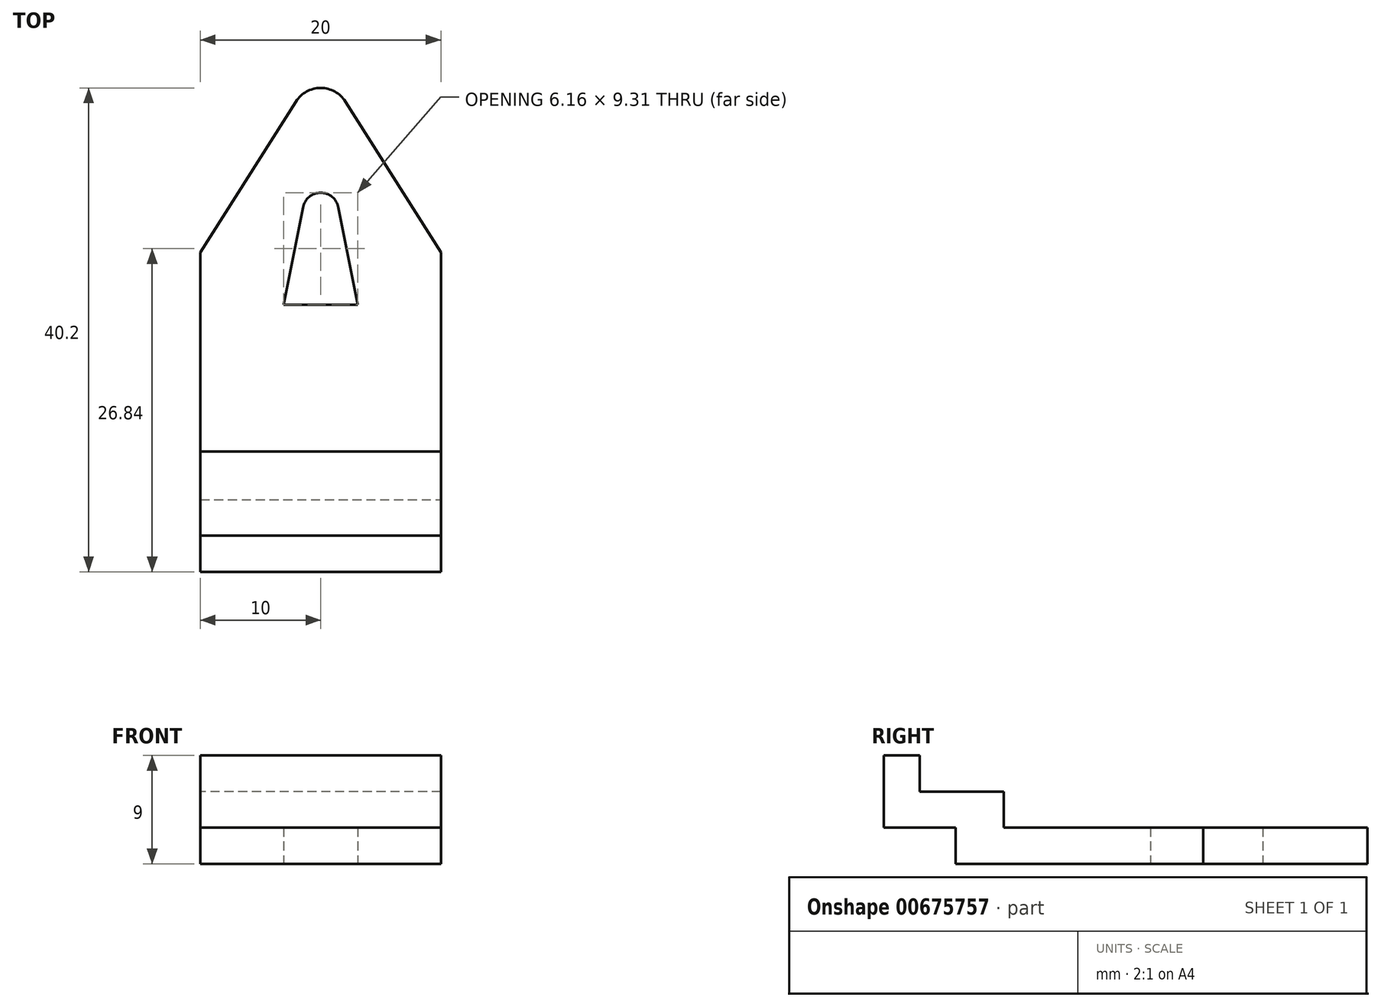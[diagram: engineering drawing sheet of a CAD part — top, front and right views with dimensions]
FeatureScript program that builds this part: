
annotation { "Feature Type Name" : "Feature", "Feature Type Description" : "" }
export const myFeature = defineFeature(function(context is Context, id is Id, definition is map)
    precondition{}
    {
        {
            var Q0;
            Q0=qCreatedBy(makeId("Top.planeOp"),FACE);
            var sketch = newSketch(context, id + "F0", { "sketchPlane" : qUnion([Q0])});
            skLineSegment(sketch, "E0", {"start": v(-2.06, -3.26) * mm, "end": v(-10, -15.78) * mm});
            skLineSegment(sketch, "E1", {"start": v(-10, -15.78) * mm, "end": v(-10, -42.32) * mm});
            skLineSegment(sketch, "E2", {"start": v(-10, -42.32) * mm, "end": v(0, -42.32) * mm});
            skArc(sketch, "E3", {"start": v(1.47, -12.03) * mm, "mid": v(0, -10.82) * mm, "end": v(-1.47, -12.03) * mm});
            skLineSegment(sketch, "E4.MirrorCS", {"start": v(10, -42.32) * mm, "end": v(0, -42.32) * mm});
            skLineSegment(sketch, "E5.MirrorCS", {"start": v(2.06, -3.26) * mm, "end": v(10, -15.78) * mm});
            skLineSegment(sketch, "E6.MirrorCS", {"start": v(10, -15.78) * mm, "end": v(10, -42.32) * mm});
            skArc(sketch, "E7", {"start": v(2.06, -3.26) * mm, "mid": v(0, -2.12) * mm, "end": v(-2.06, -3.26) * mm});
            skPoint(sketch, "E8.orphan", {"position": v(0, 0) * mm});
            skLineSegment(sketch, "E9", {"start": v(-1.47, -12.03) * mm, "end": v(-3.08, -20.14) * mm});
            skLineSegment(sketch, "E10", {"start": v(1.47, -12.03) * mm, "end": v(3.08, -20.14) * mm});
            skLineSegment(sketch, "E11", {"start": v(3.08, -20.14) * mm, "end": v(-3.08, -20.14) * mm});
            skSolve(sketch);
        }
        {
            var Q0;
            Q0=makeQuery(id+"F0.imprint","IMPRINT",FACE,{"disambiguationData":[TD([[makeQuery(id+"F0.imprint","IMPRINT",EDGE,{"derivedFrom":sQuery(id+"F0.wireOp",EDGE,"E0")}),1.0]])]});
            extrude(context, id + "F1", {"entities" : qUnion([Q0]), "depth" : 3 * mm, "offsetDistance" : 25 * mm});
        }
        {
            var Q0;
            Q0=makeQuery(id+"F1.opExtrude","CAP_FACE",FACE,{"disambiguationData":[OSD([sQuery(id+"F0.wireOp",EDGE,"E0"),sQuery(id+"F0.wireOp",EDGE,"E1"),sQuery(id+"F0.wireOp",EDGE,"E2"),sQuery(id+"F0.wireOp",EDGE,"E3"),sQuery(id+"F0.wireOp",EDGE,"E4.MirrorCS"),sQuery(id+"F0.wireOp",EDGE,"E5.MirrorCS"),sQuery(id+"F0.wireOp",EDGE,"E6.MirrorCS"),sQuery(id+"F0.wireOp",EDGE,"E7")])],"isStart":false});
            var sketch = newSketch(context, id + "F2", { "sketchPlane" : qUnion([Q0])});
            skLineSegment(sketch, "E12.bottom", {"start": v(10, -42.32) * mm, "end": v(-10, -42.32) * mm});
            skLineSegment(sketch, "E12.top", {"start": v(10, -32.32) * mm, "end": v(-10, -32.32) * mm});
            skLineSegment(sketch, "E12.left", {"start": v(10, -42.32) * mm, "end": v(10, -32.32) * mm});
            skLineSegment(sketch, "E12.right", {"start": v(-10, -42.32) * mm, "end": v(-10, -32.32) * mm});
            skSolve(sketch);
        }
        {
            var Q0;
            Q0=makeQuery(id+"F2.imprint","IMPRINT",FACE,{"disambiguationData":[TD([[makeQuery(id+"F2.imprint","IMPRINT",EDGE,{"derivedFrom":sQuery(id+"F2.wireOp",EDGE,"E12.bottom")}),1.0]])]});
            extrude(context, id + "F3", {"entities" : qUnion([Q0]), "operationType" : NewBodyOperationType.ADD, "depth" : 6 * mm, "offsetDistance" : 25 * mm});
        }
        {
            var Q0;
            Q0=makeQuery(id+"F1.opExtrude","CAP_FACE",FACE,{"disambiguationData":[OSD([sQuery(id+"F0.wireOp",EDGE,"E0"),sQuery(id+"F0.wireOp",EDGE,"E1"),sQuery(id+"F0.wireOp",EDGE,"E2"),sQuery(id+"F0.wireOp",EDGE,"E3"),sQuery(id+"F0.wireOp",EDGE,"E4.MirrorCS"),sQuery(id+"F0.wireOp",EDGE,"E5.MirrorCS"),sQuery(id+"F0.wireOp",EDGE,"E6.MirrorCS"),sQuery(id+"F0.wireOp",EDGE,"E7")])],"isStart":true});
            var sketch = newSketch(context, id + "F4", { "sketchPlane" : qUnion([Q0])});
            skLineSegment(sketch, "E13.bottom", {"start": v(-10, 42.32) * mm, "end": v(10, 42.32) * mm});
            skLineSegment(sketch, "E13.top", {"start": v(-10, 36.32) * mm, "end": v(10, 36.32) * mm});
            skLineSegment(sketch, "E13.left", {"start": v(-10, 42.32) * mm, "end": v(-10, 36.32) * mm});
            skLineSegment(sketch, "E13.right", {"start": v(10, 42.32) * mm, "end": v(10, 36.32) * mm});
            skSolve(sketch);
        }
        {
            var Q0;
            Q0 = qSketchRegion(id + "F4", true);
            extrude(context, id + "F5", {"entities" : qUnion([Q0]), "operationType" : NewBodyOperationType.REMOVE, "oppositeDirection" : true, "depth" : 3 * mm, "offsetDistance" : 25 * mm});
        }
        {
            var Q0;
            Q0=makeQuery(id+"F3.opExtrude","CAP_FACE",FACE,{"disambiguationData":[OSD([sQuery(id+"F2.wireOp",EDGE,"E12.bottom"),sQuery(id+"F2.wireOp",EDGE,"E12.top"),sQuery(id+"F2.wireOp",EDGE,"E12.left"),sQuery(id+"F2.wireOp",EDGE,"E12.right")])],"isStart":false});
            var sketch = newSketch(context, id + "F6", { "sketchPlane" : qUnion([Q0])});
            skLineSegment(sketch, "E14.bottom", {"start": v(10, -32.32) * mm, "end": v(-10, -32.32) * mm});
            skLineSegment(sketch, "E14.top", {"start": v(10, -39.32) * mm, "end": v(-10, -39.32) * mm});
            skLineSegment(sketch, "E14.left", {"start": v(10, -32.32) * mm, "end": v(10, -39.32) * mm});
            skLineSegment(sketch, "E14.right", {"start": v(-10, -32.32) * mm, "end": v(-10, -39.32) * mm});
            skSolve(sketch);
        }
        {
            var Q0;
            Q0 = qSketchRegion(id + "F6", true);
            extrude(context, id + "F7", {"entities" : qUnion([Q0]), "operationType" : NewBodyOperationType.REMOVE, "oppositeDirection" : true, "depth" : 3 * mm, "offsetDistance" : 25 * mm});
        }
    });
